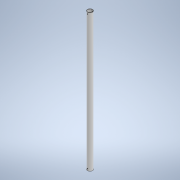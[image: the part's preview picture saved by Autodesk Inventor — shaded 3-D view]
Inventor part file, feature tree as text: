
AUTODESK INVENTOR PART (.ipt)
format: ipt  version: 2022 (Build 260153000, 153)  size: 169,984 bytes
history: native  units: mm
features: extrude x2, sketch x2
ambient origin geometry x8: Origin, YZ Plane, XZ Plane, XY Plane, X Axis, Y Axis, Z Axis, Center Point
bodies: Body1 (feature_tree)
feature tree (4):
  extrude  "Extrusion5"  Depth=18.0mm
  extrude  "Extrusion6"  Depth=10.0mm TaperAngle=0.0deg
  sketch  "Sketch2"  dims[d31=34.456mm d91=18.0mm]
  sketch  "Sketch3"  dims[d92=16.0mm d93=500.0mm d94=0.0mm d95=6.0mm d96=3.0mm d97=6.0mm d98=3.0mm d99=10.0mm d100=10.0mm d101=0.0mm d102=0.0mm]
